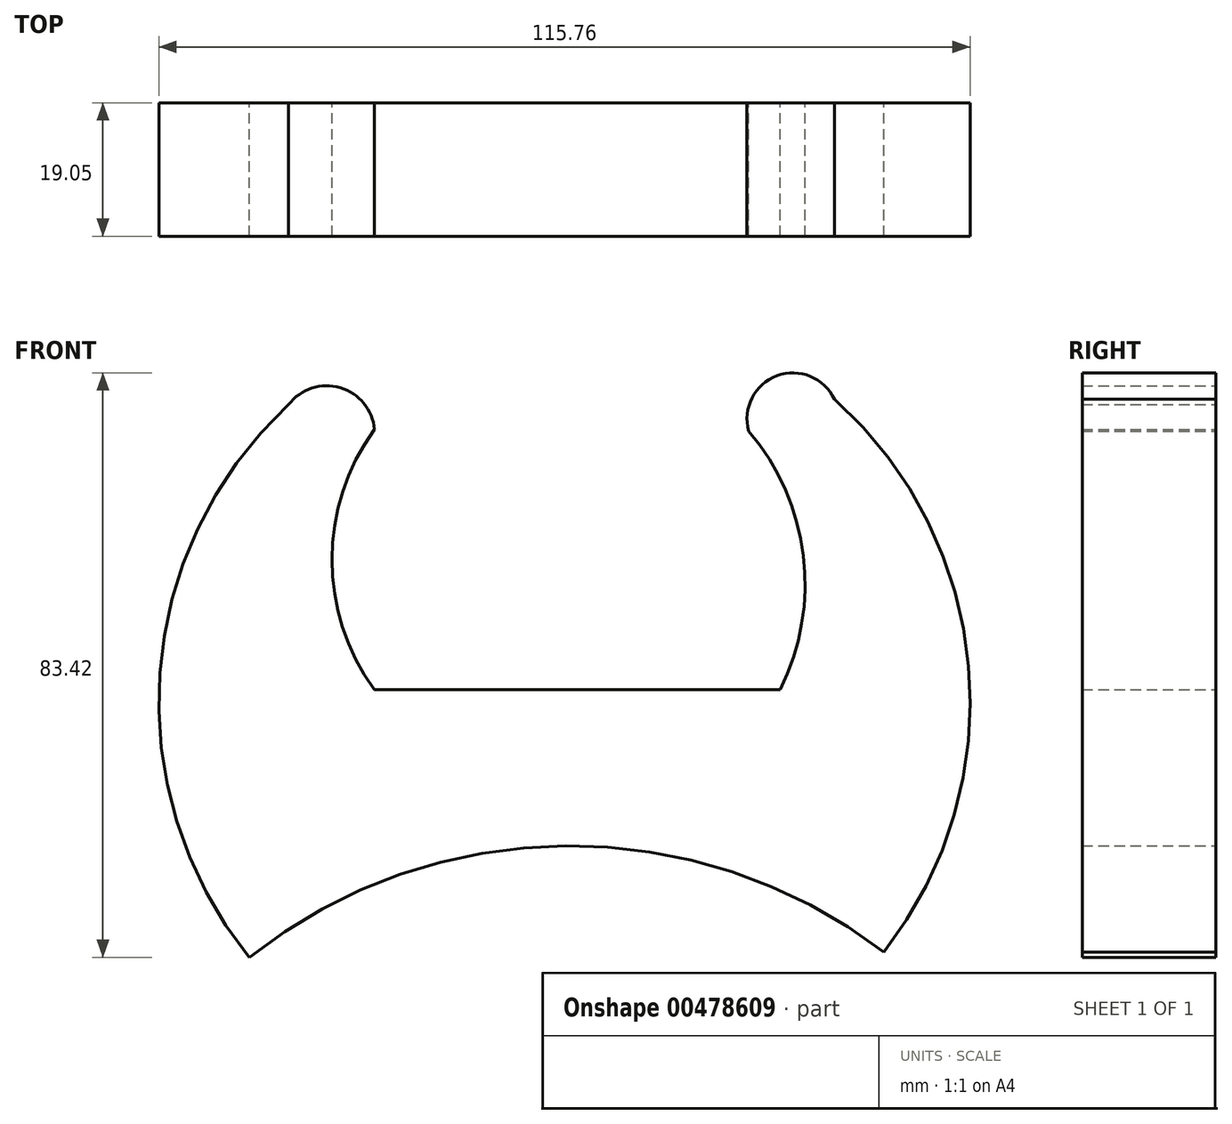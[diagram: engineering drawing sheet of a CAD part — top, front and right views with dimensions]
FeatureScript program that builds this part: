
annotation { "Feature Type Name" : "Feature", "Feature Type Description" : "" }
export const myFeature = defineFeature(function(context is Context, id is Id, definition is map)
    precondition{}
    {
        {
            var Q0;
            Q0=qCreatedBy(makeId("Front.planeOp"),FACE);
            var sketch = newSketch(context, id + "F0", { "sketchPlane" : qUnion([Q0])});
            skArc(sketch, "E0", {"start": v(-39.35, 42.45) * mm, "mid": v(-57.74, 4.11) * mm, "end": v(-44.97, -36.44) * mm});
            skLineSegment(sketch, "E1", {"start": v(30.77, 1.78) * mm, "end": v(-14.45, 1.78) * mm});
            skLineSegment(sketch, "E2", {"start": v(-14.45, 1.78) * mm, "end": v(-27.15, 1.78) * mm});
            skArc(sketch, "E3.trimOffspring", {"start": v(45.57, -35.69) * mm, "mid": v(57.66, 5.15) * mm, "end": v(38.53, 43.2) * mm});
            skArc(sketch, "E4", {"start": v(-27.11, 38.9) * mm, "mid": v(-33.18, 20.34) * mm, "end": v(-27.15, 1.78) * mm});
            skArc(sketch, "E5", {"start": v(30.77, 1.78) * mm, "mid": v(34.1, 20.9) * mm, "end": v(26.28, 38.67) * mm});
            skArc(sketch, "E6", {"start": v(45.57, -35.69) * mm, "mid": v(0.17, -20.53) * mm, "end": v(-44.97, -36.44) * mm});
            skArc(sketch, "E7", {"start": v(38.53, 43.2) * mm, "mid": v(30.32, 46.57) * mm, "end": v(26.28, 38.67) * mm});
            skArc(sketch, "E8", {"start": v(-27.11, 38.9) * mm, "mid": v(-32.01, 44.88) * mm, "end": v(-39.35, 42.45) * mm});
            skLineSegment(sketch, "E9", {"start": v(-1.75, -5.12) * mm, "end": v(-1.75, -12.44) * mm});
            skLineSegment(sketch, "E10", {"start": v(-1.75, -12.44) * mm, "end": v(5.37, -12.44) * mm});
            skLineSegment(sketch, "E11", {"start": v(5.37, -12.44) * mm, "end": v(5.37, -5.12) * mm});
            skLineSegment(sketch, "E12", {"start": v(-1.75, -5.12) * mm, "end": v(5.37, -5.12) * mm});
            skSolve(sketch);
        }
        {
            var Q0;
            Q0=qSketchRegion(id+"F0",true);
            var Q1;
            Q1=makeQuery(id+"F0.imprint","IMPRINT",FACE,{"disambiguationData":[TD([[makeQuery(id+"F0.imprint","IMPRINT",EDGE,{"derivedFrom":sQuery(id+"F0.wireOp",EDGE,"E9")}),1.0]])]});
            extrude(context, id + "F1", {"entities" : qUnion([Q0, Q1]), "depth" : 19.05 * mm, "offsetDistance" : 25.4 * mm});
        }
    });
